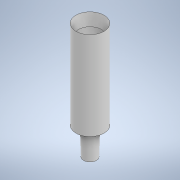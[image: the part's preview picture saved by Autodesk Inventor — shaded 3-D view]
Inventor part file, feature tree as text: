
AUTODESK INVENTOR PART (.ipt)
format: ipt  version: 2020 (Build 240168000, 168)  size: 115,200 bytes
history: native  units: in
note: dims shown in document units (in); Inventor stores cm internally (conversion verified against a paired STEP export)
features: revolve x1, sketch x1
ambient origin geometry x8: Origin, YZ Plane, XZ Plane, XY Plane, X Axis, Y Axis, Z Axis, Center Point
bodies: Solid1 (feature_tree)
feature tree (2):
  revolve  "Revolution1"  [1 undecoded]
  sketch  "Sketch1"  dims[d0=0.0787in d6=0.3346in d20=45.0deg d21=90.0deg]
note: 1 required parameter value undecoded (feature->parameter linkage not recoverable at this tier; creation-order binding heuristic only, values carry confidence <= 0.55)
